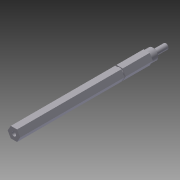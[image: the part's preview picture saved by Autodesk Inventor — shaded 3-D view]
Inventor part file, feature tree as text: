
AUTODESK INVENTOR PART (.ipt)
format: ipt  version: 2013 (Build 170138000, 138)  size: 120,320 bytes
history: native  units: in
note: dims shown in document units (in); Inventor stores cm internally (conversion verified against a paired STEP export)
features: other x2, extrude x2, sketch x2, imported_body x1
ambient origin geometry x8: Origin, YZ Plane, XZ Plane, XY Plane, X Axis, Y Axis, Z Axis, Center Point
feature tree (7):
  other  "Supershifter Long Hex Output Shaft"
  other  "super_d17"
  imported_body  "Base1"
  extrude  "Extrusion1"  Depth=0.75in
  extrude  "Extrusion2"  Depth=0.75in
  sketch  "Sketch1"  dims[d0=0.5in d2=0.75in]
  sketch  "Sketch2"  dims[d3=0.313in d4=0.0in d5=0.75in d8=2.938in d9=0.0in]
